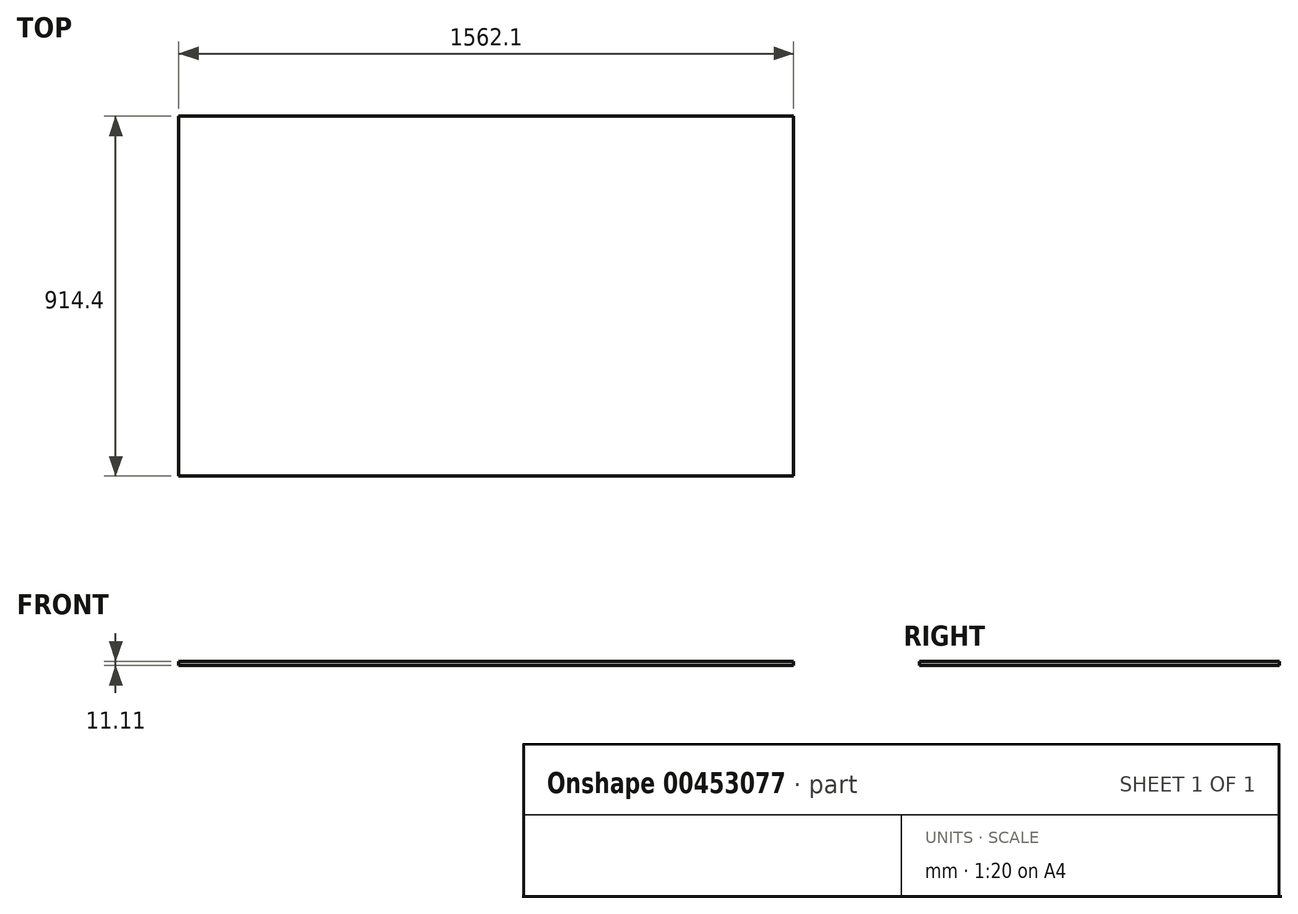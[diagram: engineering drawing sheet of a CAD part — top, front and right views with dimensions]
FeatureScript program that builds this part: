
annotation { "Feature Type Name" : "Feature", "Feature Type Description" : "" }
export const myFeature = defineFeature(function(context is Context, id is Id, definition is map)
    precondition{}
    {
        {
            var Q0;
            Q0=qCreatedBy(makeId("Top.planeOp"),FACE);
            var sketch = newSketch(context, id + "F0", { "sketchPlane" : qUnion([Q0])});
            skLineSegment(sketch, "E0.bottom", {"start": v(781.05, 457.2) * mm, "end": v(-781.05, 457.2) * mm});
            skLineSegment(sketch, "E0.top", {"start": v(781.05, -457.2) * mm, "end": v(-781.05, -457.2) * mm});
            skLineSegment(sketch, "E0.left", {"start": v(781.05, 457.2) * mm, "end": v(781.05, -457.2) * mm});
            skLineSegment(sketch, "E0.right", {"start": v(-781.05, 457.2) * mm, "end": v(-781.05, -457.2) * mm});
            skPoint(sketch, "E0.middle", {"position": v(0, 0) * mm});
            skSolve(sketch);
        }
        {
            var Q0;
            Q0 = qSketchRegion(id + "F0", true);
            extrude(context, id + "F1", {"entities" : qUnion([Q0]), "depth" : 11.1 * mm, "offsetDistance" : 25.4 * mm});
        }
    });
